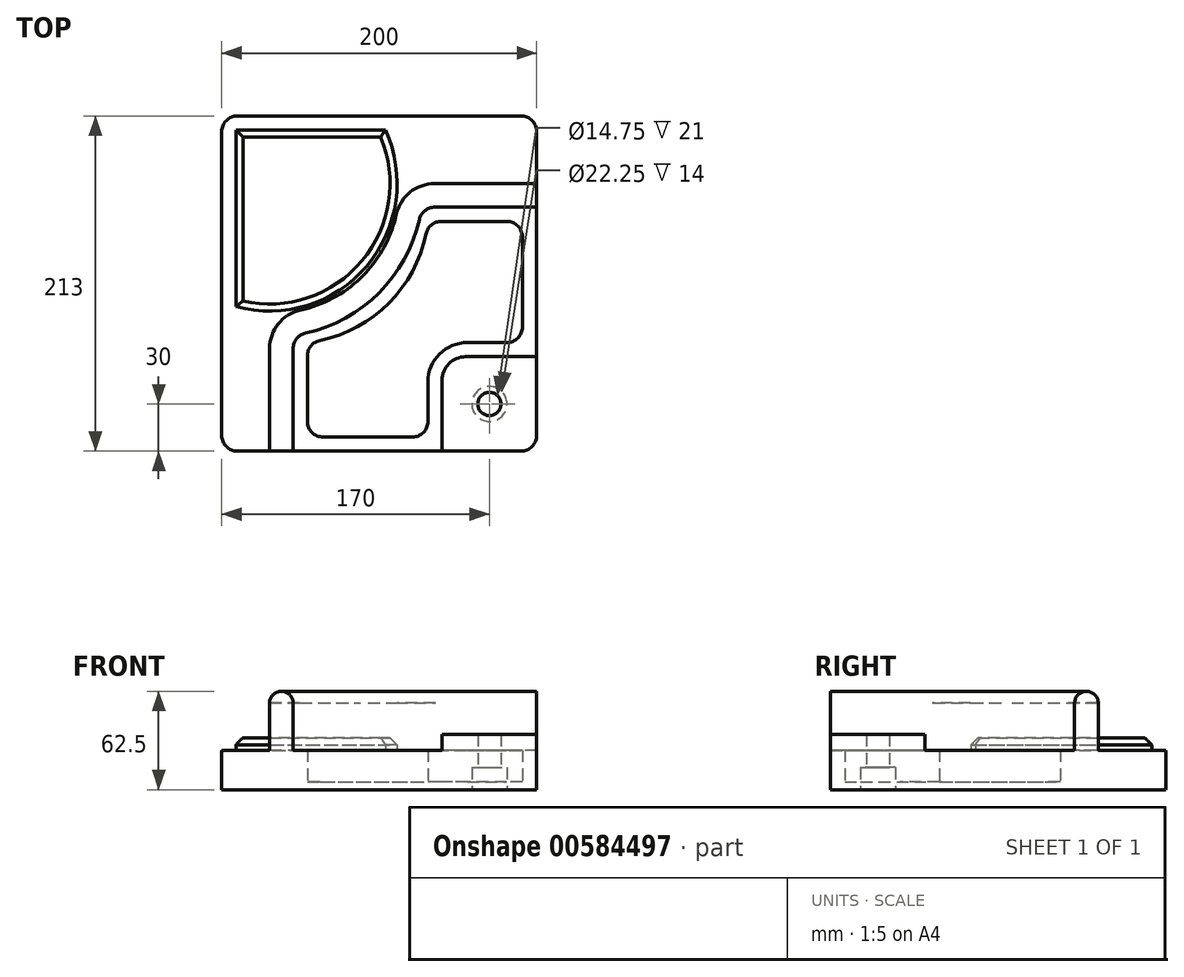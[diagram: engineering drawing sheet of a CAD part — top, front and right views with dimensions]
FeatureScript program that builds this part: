
annotation { "Feature Type Name" : "Feature", "Feature Type Description" : "" }
export const myFeature = defineFeature(function(context is Context, id is Id, definition is map)
    precondition{}
    {
        {
            var Q0;
            Q0=qCreatedBy(makeId("Top.planeOp"),FACE);
            var sketch = newSketch(context, id + "F0", { "sketchPlane" : qUnion([Q0])});
            skLineSegment(sketch, "E0.bottom", {"start": v(-90, 106.5) * mm, "end": v(90, 106.5) * mm});
            skLineSegment(sketch, "E0.top", {"start": v(-90, -106.5) * mm, "end": v(90, -106.5) * mm});
            skLineSegment(sketch, "E0.left", {"start": v(-100, 96.5) * mm, "end": v(-100, -96.5) * mm});
            skLineSegment(sketch, "E0.right", {"start": v(100, 96.5) * mm, "end": v(100, -96.5) * mm});
            skPoint(sketch, "E0.middle", {"position": v(0, 0) * mm});
            skLineSegment(sketch, "E1", {"start": v(100, -46.5) * mm, "end": v(55, -46.5) * mm});
            skLineSegment(sketch, "E2", {"start": v(40, -61.5) * mm, "end": v(40, -106.5) * mm});
            skLineSegment(sketch, "E3", {"start": v(100, 63.5) * mm, "end": v(35.74, 63.5) * mm});
            skLineSegment(sketch, "E4", {"start": v(-69.62, -41.86) * mm, "end": v(-69.62, -106.5) * mm});
            skPoint(sketch, "E5.visualSharp", {"position": v(40, -46.5) * mm});
            skArc(sketch, "E5.filletArc", {"start": v(55, -46.5) * mm, "mid": v(44.4, -50.9) * mm, "end": v(40, -61.5) * mm});
            skLineSegment(sketch, "E6", {"start": v(31, -87.5) * mm, "end": v(31, -62.5) * mm});
            skLineSegment(sketch, "E7", {"start": v(56, -37.5) * mm, "end": v(81, -37.5) * mm});
            skLineSegment(sketch, "E8", {"start": v(-45.62, -87.5) * mm, "end": v(-45.62, -46) * mm});
            skLineSegment(sketch, "E9", {"start": v(-35.62, -97.5) * mm, "end": v(21, -97.5) * mm});
            skPoint(sketch, "E10.orphan", {"position": v(31, -106.5) * mm});
            skPoint(sketch, "E11.orphan", {"position": v(-45.62, -106.5) * mm});
            skLineSegment(sketch, "E12", {"start": v(91, -27.5) * mm, "end": v(91, 29.5) * mm});
            skPoint(sketch, "E13.orphan", {"position": v(100, -37.5) * mm});
            skLineSegment(sketch, "E14", {"start": v(81, 39.5) * mm, "end": v(39.54, 39.5) * mm});
            skPoint(sketch, "E15.visualSharp", {"position": v(-45.62, -97.5) * mm});
            skArc(sketch, "E15.filletArc", {"start": v(-45.62, -87.5) * mm, "mid": v(-42.7, -94.57) * mm, "end": v(-35.62, -97.5) * mm});
            skPoint(sketch, "E16.visualSharp", {"position": v(31, -97.5) * mm});
            skArc(sketch, "E16.filletArc", {"start": v(21, -97.5) * mm, "mid": v(28.07, -94.57) * mm, "end": v(31, -87.5) * mm});
            skPoint(sketch, "E17.visualSharp", {"position": v(91, -37.5) * mm});
            skArc(sketch, "E17.filletArc", {"start": v(81, -37.5) * mm, "mid": v(88.07, -34.57) * mm, "end": v(91, -27.5) * mm});
            skPoint(sketch, "E18.visualSharp", {"position": v(91, 39.5) * mm});
            skArc(sketch, "E18.filletArc", {"start": v(91, 29.5) * mm, "mid": v(88.07, 36.57) * mm, "end": v(81, 39.5) * mm});
            skPoint(sketch, "E19.visualSharp", {"position": v(31, -37.5) * mm});
            skArc(sketch, "E19.filletArc", {"start": v(56, -37.5) * mm, "mid": v(38.32, -44.82) * mm, "end": v(31, -62.5) * mm});
            skArc(sketch, "E20", {"start": v(-37.67, -36.22) * mm, "mid": v(6.16, -12.43) * mm, "end": v(29.75, 31.5) * mm});
            skPoint(sketch, "E21.visualSharp", {"position": v(-45.62, -37.5) * mm});
            skArc(sketch, "E21.filletArc", {"start": v(-37.67, -36.22) * mm, "mid": v(-43.39, -39.7) * mm, "end": v(-45.62, -46) * mm});
            skPoint(sketch, "E22.visualSharp", {"position": v(31, 39.5) * mm});
            skArc(sketch, "E22.filletArc", {"start": v(39.54, 39.5) * mm, "mid": v(33.22, 37.25) * mm, "end": v(29.75, 31.5) * mm});
            skPoint(sketch, "E23.visualSharp", {"position": v(100, 106.5) * mm});
            skArc(sketch, "E23.filletArc", {"start": v(100, 96.5) * mm, "mid": v(97.07, 103.57) * mm, "end": v(90, 106.5) * mm});
            skPoint(sketch, "E24.visualSharp", {"position": v(-100, 106.5) * mm});
            skArc(sketch, "E24.filletArc", {"start": v(-90, 106.5) * mm, "mid": v(-97.07, 103.57) * mm, "end": v(-100, 96.5) * mm});
            skPoint(sketch, "E25.visualSharp", {"position": v(-100, -106.5) * mm});
            skArc(sketch, "E25.filletArc", {"start": v(-100, -96.5) * mm, "mid": v(-97.07, -103.57) * mm, "end": v(-90, -106.5) * mm});
            skPoint(sketch, "E26.visualSharp", {"position": v(100, -106.5) * mm});
            skArc(sketch, "E26.filletArc", {"start": v(90, -106.5) * mm, "mid": v(97.07, -103.57) * mm, "end": v(100, -96.5) * mm});
            skLineSegment(sketch, "E27", {"start": v(-54.62, -106.5) * mm, "end": v(-54.62, -41.3) * mm});
            skLineSegment(sketch, "E28", {"start": v(100, 48.5) * mm, "end": v(35.26, 48.5) * mm});
            skArc(sketch, "E29", {"start": v(-50.4, -17.53) * mm, "mid": v(-10.73, 4.6) * mm, "end": v(11.41, 44.27) * mm});
            skArc(sketch, "E30.filletArc", {"start": v(-50.4, -17.53) * mm, "mid": v(-64.24, -26.36) * mm, "end": v(-69.62, -41.86) * mm});
            skPoint(sketch, "E31.visualSharp", {"position": v(13.66, 63.5) * mm});
            skArc(sketch, "E31.filletArc", {"start": v(35.74, 63.5) * mm, "mid": v(20.23, 58.11) * mm, "end": v(11.41, 44.27) * mm});
            skArc(sketch, "E32", {"start": v(-91, -14.63) * mm, "mid": v(-7.8, 11.17) * mm, "end": v(3.9, 97.5) * mm});
            skLineSegment(sketch, "E33", {"start": v(-91, 97.5) * mm, "end": v(-91, -14.63) * mm});
            skLineSegment(sketch, "E34", {"start": v(-91, 97.5) * mm, "end": v(3.9, 97.5) * mm});
            skPoint(sketch, "E35.orphan", {"position": v(31, 48.5) * mm});
            skPoint(sketch, "E36.visualSharp", {"position": v(-54.62, -32.92) * mm});
            skPoint(sketch, "E37.visualSharp", {"position": v(23.52, 48.5) * mm});
            skArc(sketch, "E38", {"start": v(-46.78, -31.53) * mm, "mid": v(-0.1, -5.98) * mm, "end": v(25.5, 40.66) * mm});
            skArc(sketch, "E39.filletArc", {"start": v(-46.78, -31.53) * mm, "mid": v(-52.42, -35.03) * mm, "end": v(-54.62, -41.3) * mm});
            skPoint(sketch, "E40.visualSharp", {"position": v(26.9, 48.5) * mm});
            skArc(sketch, "E40.filletArc", {"start": v(35.26, 48.5) * mm, "mid": v(29, 46.3) * mm, "end": v(25.5, 40.66) * mm});
            skLineSegment(sketch, "E41", {"start": v(70, -106.5) * mm, "end": v(70, -46.5) * mm, "construction": true});
            skLineSegment(sketch, "E42", {"start": v(40, -76.5) * mm, "end": v(100, -76.5) * mm, "construction": true});
            skPoint(sketch, "E43", {"position": v(70, -76.5) * mm});
            skSolve(sketch);
        }
        {
            var Q0;
            {var subQ1=sQuery(id+"F0.wireOp",EDGE,"E1");Q0=makeQuery(id+"F0.imprint","IMPRINT",FACE,{"disambiguationData":[TD([[makeQuery(id+"F0.imprint","IMPRINT",EDGE,{"derivedFrom":subQ1}),1.0]])]});}
            extrude(context, id + "F1", {"entities" : qUnion([Q0]), "depth" : 35 * mm, "offsetDistance" : 25 * mm});
        }
        {
            var Q0;
            {var subQ3=sQuery(id+"F0.wireOp",EDGE,"E1");Q0=makeQuery(id+"F0.imprint","IMPRINT",FACE,{"disambiguationData":[TD([[makeQuery(id+"F0.imprint","IMPRINT",EDGE,{"derivedFrom":subQ3}),-1.0]])]});}
            extrude(context, id + "F2", {"entities" : qUnion([Q0]), "operationType" : NewBodyOperationType.ADD, "depth" : 25 * mm, "offsetDistance" : 25 * mm});
        }
        {
            var Q0;
            {var subQ2=sQuery(id+"F0.wireOp",EDGE,"E3");Q0=makeQuery(id+"F0.imprint","IMPRINT",FACE,{"disambiguationData":[TD([[makeQuery(id+"F0.imprint","IMPRINT",EDGE,{"derivedFrom":subQ2}),1.0]])]});}
            extrude(context, id + "F3", {"entities" : qUnion([Q0]), "operationType" : NewBodyOperationType.ADD, "depth" : 55 * mm, "offsetDistance" : 25 * mm});
        }
        {
            var Q0;
            Q0=makeQuery(id+"F0.imprint","IMPRINT",FACE,{"disambiguationData":[TD([[makeQuery(id+"F0.imprint","IMPRINT",EDGE,{"derivedFrom":sQuery(id+"F0.wireOp",EDGE,"E0.bottom")}),-1.0]])]});
            extrude(context, id + "F4", {"entities" : qUnion([Q0]), "operationType" : NewBodyOperationType.ADD, "depth" : 25 * mm, "offsetDistance" : 25 * mm});
        }
        {
            var Q0;
            Q0=makeQuery(id+"F0.imprint","IMPRINT",FACE,{"disambiguationData":[TD([[makeQuery(id+"F0.imprint","IMPRINT",EDGE,{"derivedFrom":sQuery(id+"F0.wireOp",EDGE,"E32")}),1.0]])]});
            extrude(context, id + "F5", {"entities" : qUnion([Q0]), "operationType" : NewBodyOperationType.ADD, "depth" : 33 * mm, "offsetDistance" : 25 * mm});
        }
        {
            var Q0;
            Q0=makeQuery(id+"F0.imprint","IMPRINT",FACE,{"disambiguationData":[TD([[makeQuery(id+"F0.imprint","IMPRINT",EDGE,{"derivedFrom":sQuery(id+"F0.wireOp",EDGE,"E6")}),1.0]])]});
            extrude(context, id + "F6", {"entities" : qUnion([Q0]), "operationType" : NewBodyOperationType.ADD, "depth" : 5 * mm, "offsetDistance" : 25 * mm});
        }
        {
            var Q0;
            {var subQ0=sQuery(id+"F0.wireOp",EDGE,"E0.top");Q0=makeQuery(id+"F4.boolean.opBoolean","MERGE",FACE,{"derivedFrom":[makeQuery(id+"F3.boolean.opBoolean","MERGE",FACE,{"derivedFrom":[makeQuery(id+"F2.boolean.opBoolean","MERGE",FACE,{"derivedFrom":[makeQuery(id+"F1.opExtrude","SWEPT_FACE",FACE,{"disambiguationData":[OSD([subQ0])]}),makeQuery(id+"F2.opExtrude","SWEPT_FACE",FACE,{"disambiguationData":[OSD([subQ0])]})]}),makeQuery(id+"F3.opExtrude","SWEPT_FACE",FACE,{"disambiguationData":[OSD([subQ0])]})]}),makeQuery(id+"F4.opExtrude","SWEPT_FACE",FACE,{"disambiguationData":[OSD([subQ0])]})]});}
            var sketch = newSketch(context, id + "F7", { "sketchPlane" : qUnion([Q0])});
            skLineSegment(sketch, "E44.0", {"start": v(-69.62, 55) * mm, "end": v(-54.62, 55) * mm});
            skArc(sketch, "E45", {"start": v(-54.62, 55) * mm, "mid": v(-62.12, 62.5) * mm, "end": v(-69.62, 55) * mm});
            skSolve(sketch);
        }
        {
            var Q0;
            Q0=makeQuery(id+"F7.imprint","IMPRINT",FACE,{"disambiguationData":[TD([[makeQuery(id+"F7.imprint","IMPRINT",EDGE,{"derivedFrom":sQuery(id+"F7.wireOp",EDGE,"E44.0")}),1.0]])]});
            var Q1;
            Q1=makeQuery(id+"F3.opExtrude","CAP_EDGE",EDGE,{"disambiguationData":[OSD([sQuery(id+"F0.wireOp",EDGE,"E27")])],"isStart":false});
            var Q2;
            Q2=makeQuery(id+"F3.opExtrude","CAP_EDGE",EDGE,{"disambiguationData":[OSD([sQuery(id+"F0.wireOp",EDGE,"E38")])],"isStart":false});
            var Q3;
            Q3=makeQuery(id+"F3.opExtrude","CAP_EDGE",EDGE,{"disambiguationData":[OSD([sQuery(id+"F0.wireOp",EDGE,"E39.filletArc")])],"isStart":false});
            var Q4;
            Q4=makeQuery(id+"F3.opExtrude","CAP_EDGE",EDGE,{"disambiguationData":[OSD([sQuery(id+"F0.wireOp",EDGE,"E40.filletArc")])],"isStart":false});
            var Q5;
            Q5=makeQuery(id+"F3.opExtrude","CAP_EDGE",EDGE,{"disambiguationData":[OSD([sQuery(id+"F0.wireOp",EDGE,"E28")])],"isStart":false});
            sweep(context, id + "F8", {"operationType" : NewBodyOperationType.ADD, "profiles" : qUnion([Q0]), "path" : qUnion([Q1, Q2, Q3, Q4, Q5])});
        }
        {
            var Q0;
            Q0=makeQuery(id+"F5.opExtrude","CAP_FACE",FACE,{"disambiguationData":[OSD([sQuery(id+"F0.wireOp",EDGE,"E32"),sQuery(id+"F0.wireOp",EDGE,"E33"),sQuery(id+"F0.wireOp",EDGE,"E34")])],"isStart":false});
            chamfer(context, id + "F9", {"entities" : qUnion([Q0]), "width" : 4.5 * mm, "tangentPropagation" : true});
        }
        {
            var Q0;
            Q0=sQuery(id+"F0.wireOp",VERTEX,"E43");
            var Q1;
            Q1=makeQuery(id+"F1.opExtrude","SWEPT_BODY",BODY,{"disambiguationData":[OSD([sQuery(id+"F0.wireOp",EDGE,"E0.top"),sQuery(id+"F0.wireOp",EDGE,"E0.right"),sQuery(id+"F0.wireOp",EDGE,"E1"),sQuery(id+"F0.wireOp",EDGE,"E2"),sQuery(id+"F0.wireOp",EDGE,"E5.filletArc"),sQuery(id+"F0.wireOp",EDGE,"E26.filletArc")])]});
            hole(context, id + "F10", {"style" : HoleStyle.C_BORE, "endStyle" : HoleEndStyle.THROUGH, "oppositeDirection" : true, "standardTappedOrClearance" : lookupTablePath({ "standard" : "ISO", "fit" : "Close", "size" : "M14", "type" : "Clearance" }), "standardBlindInLast" : lookupTablePath({ "fit" : "Close", "standard" : "ISO", "size" : "M14", "type" : "Clearance" }), "holeDiameter" : 14.75 * mm, "cBoreDiameter" : 22.25 * mm, "cBoreDepth" : 14 * mm, "majorDiameter" : 5 * mm, "isTappedThrough" : true, "tappedDepth" : 12 * mm, "tapClearance" : 3, "locations" : qUnion([Q0]), "scope" : qUnion([Q1])});
        }
    });
